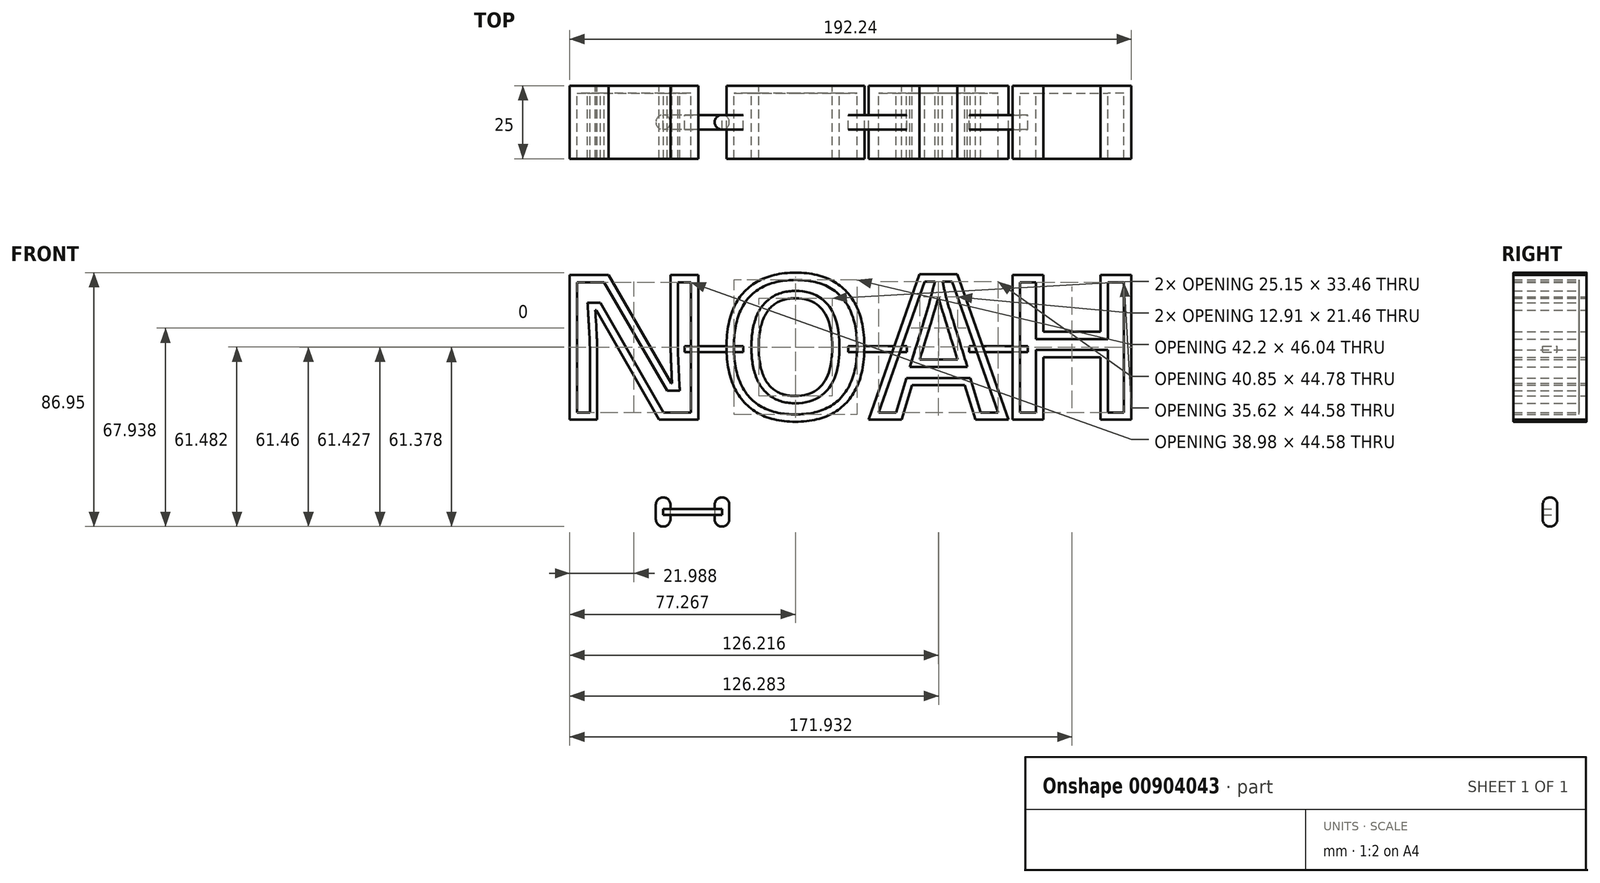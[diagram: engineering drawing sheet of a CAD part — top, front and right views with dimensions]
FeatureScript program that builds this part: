
annotation { "Feature Type Name" : "Feature", "Feature Type Description" : "" }
export const myFeature = defineFeature(function(context is Context, id is Id, definition is map)
    precondition{}
    {
        {
            var Q0;
            Q0=qCreatedBy(makeId("Front.planeOp"),FACE);
            var sketch = newSketch(context, id + "F0", { "sketchPlane" : qUnion([Q0])});
            skText(sketch, "E0", { "text": "O", "fontName": "OpenSans-Bold.ttf"});
            skText(sketch, "E1", { "text": "A", "fontName": "OpenSans-Bold.ttf"});
            skText(sketch, "E2", { "text": "H", "fontName": "OpenSans-Bold.ttf"});
            skText(sketch, "E3", { "text": "N", "fontName": "OpenSans-Bold.ttf"});
            const initialGuessF0  = {"E0": [-0.03252, 0, 1, 0, 0.05], "E1": [0.03031, 0, 1, 0, 0.05], "E2": [0.09753, 0, 1, 0, 0.05], "E3": [-0.10159, 0, 1, 0, 0.05]};
            skSetInitialGuess(sketch, initialGuessF0);
            skSolve(sketch);
        }
        {
            var Q0;
            Q0 = qSketchRegion(id + "F0", true);
            extrude(context, id + "F1", {"entities" : qUnion([Q0]), "endBound" : BoundingType.SYMMETRIC, "depth" : 25 * mm, "offsetDistance" : 25 * mm});
        }
        {
            var Q0;
            Q0=qCreatedBy(makeId("Front.planeOp"),FACE);
            var sketch = newSketch(context, id + "F2", { "sketchPlane" : qUnion([Q0])});
            skLineSegment(sketch, "E4.bottom", {"start": v(-65.87, -26.6) * mm, "end": v(-60.87, -26.6) * mm});
            skLineSegment(sketch, "E4.top", {"start": v(-65.87, -36.6) * mm, "end": v(-60.87, -36.6) * mm});
            skLineSegment(sketch, "E4.left", {"start": v(-65.87, -26.6) * mm, "end": v(-65.87, -36.6) * mm});
            skLineSegment(sketch, "E4.right", {"start": v(-60.87, -26.6) * mm, "end": v(-60.87, -30.6) * mm});
            skLineSegment(sketch, "E5.bottom", {"start": v(-45.73, -26.6) * mm, "end": v(-40.73, -26.6) * mm});
            skLineSegment(sketch, "E5.top", {"start": v(-45.73, -36.6) * mm, "end": v(-40.73, -36.6) * mm});
            skLineSegment(sketch, "E5.left", {"start": v(-45.73, -26.6) * mm, "end": v(-45.73, -30.6) * mm});
            skLineSegment(sketch, "E5.right", {"start": v(-40.73, -26.6) * mm, "end": v(-40.73, -36.6) * mm});
            skLineSegment(sketch, "E6", {"start": v(-63.37, -26.6) * mm, "end": v(-63.37, -36.6) * mm});
            skLineSegment(sketch, "E7", {"start": v(-43.23, -36.6) * mm, "end": v(-43.23, -26.6) * mm});
            skLineSegment(sketch, "E8", {"start": v(-60.87, -30.6) * mm, "end": v(-45.73, -30.6) * mm});
            skLineSegment(sketch, "E9", {"start": v(-60.87, -32.6) * mm, "end": v(-45.73, -32.6) * mm});
            skLineSegment(sketch, "E10.trimOffspring", {"start": v(-60.87, -32.6) * mm, "end": v(-60.87, -36.6) * mm});
            skLineSegment(sketch, "E11.trimOffspring", {"start": v(-45.73, -32.6) * mm, "end": v(-45.73, -36.6) * mm});
            skLineSegment(sketch, "E12", {"start": v(-63.37, -30.6) * mm, "end": v(-43.23, -30.6) * mm});
            skLineSegment(sketch, "E13", {"start": v(-43.23, -32.6) * mm, "end": v(-63.37, -32.6) * mm});
            skSolve(sketch);
        }
        {
            var Q0;
            {var subQ0=sQuery(id+"F2.wireOp",EDGE,"E4.left");Q0=makeQuery(id+"F2.imprint","IMPRINT",FACE,{"disambiguationData":[TD([[makeQuery(id+"F2.imprint","IMPRINT",EDGE,{"derivedFrom":subQ0}),1.0]])]});}
            var Q1;
            Q1=sQuery(id+"F2.wireOp",EDGE,"E6");
            revolve(context, id + "F3", {"surfaceOperationType" : NewSurfaceOperationType.NEW, "entities" : qUnion([Q0]), "axis" : qUnion([Q1]), "revolveType" : RevolveType.FULL});
        }
        {
            var Q0;
            {var subQ0=sQuery(id+"F2.wireOp",EDGE,"E5.right");Q0=makeQuery(id+"F2.imprint","IMPRINT",FACE,{"disambiguationData":[TD([[makeQuery(id+"F2.imprint","IMPRINT",EDGE,{"derivedFrom":subQ0}),-1.0]])]});}
            var Q1;
            Q1=sQuery(id+"F2.wireOp",EDGE,"E7");
            revolve(context, id + "F4", {"surfaceOperationType" : NewSurfaceOperationType.NEW, "entities" : qUnion([Q0]), "axis" : qUnion([Q1]), "revolveType" : RevolveType.FULL});
        }
        {
            var Q0;
            {var subQ0=sQuery(id+"F2.wireOp",EDGE,"E12");var subQ2=sQuery(id+"F2.wireOp",EDGE,"E6");var subQ3=makeQuery(id+"F2.imprint","INTERSECT",VERTEX,{"derivedFrom":[subQ2,subQ0]});Q0=makeQuery(id+"F2.imprint","IMPRINT",FACE,{"disambiguationData":[TD([[makeQuery(id+"F2.imprint","IMPRINT",EDGE,{"disambiguationData":[TD([[subQ3,-1.0]])],"derivedFrom":subQ2}),1.0]])]});}
            extrude(context, id + "F5", {"entities" : qUnion([Q0]), "endBound" : BoundingType.SYMMETRIC, "depth" : 5 * mm, "offsetDistance" : 25 * mm});
        }
        {
            var Q0;
            Q0=makeQuery(id+"F3.opRevolve","SWEPT_FACE",FACE,{"disambiguationData":[OSD([sQuery(id+"F2.wireOp",EDGE,"E4.bottom")])]});
            var Q1;
            Q1=makeQuery(id+"F4.opRevolve","SWEPT_FACE",FACE,{"disambiguationData":[OSD([sQuery(id+"F2.wireOp",EDGE,"E5.bottom")])]});
            var Q2;
            Q2=makeQuery(id+"F4.opRevolve","SWEPT_FACE",FACE,{"disambiguationData":[OSD([sQuery(id+"F2.wireOp",EDGE,"E5.top")])]});
            var Q3;
            Q3=makeQuery(id+"F3.opRevolve","SWEPT_FACE",FACE,{"disambiguationData":[OSD([sQuery(id+"F2.wireOp",EDGE,"E4.top")])]});
            fillet(context, id + "F6", {"entities" : qUnion([Q0, Q1, Q2, Q3]), "radius" : 2.5 * mm, "tangentPropagation" : true, "allowEdgeOverflow" : false});
        }
        {
            var Q0;
            Q0=makeQuery(id+"F5.opExtrude","SWEPT_BODY",BODY,{"disambiguationData":[OSD([sQuery(id+"F2.wireOp",EDGE,"E6"),sQuery(id+"F2.wireOp",EDGE,"E7"),sQuery(id+"F2.wireOp",EDGE,"E12"),sQuery(id+"F2.wireOp",EDGE,"E13")])]});
            transform(context, id + "F7", {"entities" : qUnion([Q0]), "transformType" : TransformType.COPY});
        }
        {
            var Q0;
            Q0=makeQuery(id+"F7.opPattern","COPY",BODY,{"derivedFrom":makeQuery(id+"F5.opExtrude","SWEPT_BODY",BODY,{"disambiguationData":[OSD([sQuery(id+"F2.wireOp",EDGE,"E6"),sQuery(id+"F2.wireOp",EDGE,"E7"),sQuery(id+"F2.wireOp",EDGE,"E12"),sQuery(id+"F2.wireOp",EDGE,"E13")])]}),"instanceName":"1"});
            transform(context, id + "F8", {"entities" : qUnion([Q0]), "transformType" : TransformType.TRANSLATION_3D, "dx" : 7.3 * mm, "dy" : 0 * mm, "dz" : 55.8 * mm, "makeCopy" : false});
        }
        {
            var Q0;
            Q0=makeQuery(id+"F1.opExtrude","SWEPT_BODY",BODY,{"disambiguationData":[OSD([sQuery(id+"F0.wireOp",EDGE,"E0.sketch_text.stroke-0"),sQuery(id+"F0.wireOp",EDGE,"E0.sketch_text.stroke-1"),sQuery(id+"F0.wireOp",EDGE,"E0.sketch_text.stroke-2"),sQuery(id+"F0.wireOp",EDGE,"E0.sketch_text.stroke-3"),sQuery(id+"F0.wireOp",EDGE,"E0.sketch_text.stroke-4"),sQuery(id+"F0.wireOp",EDGE,"E0.sketch_text.stroke-5"),sQuery(id+"F0.wireOp",EDGE,"E0.sketch_text.stroke-6"),sQuery(id+"F0.wireOp",EDGE,"E0.sketch_text.stroke-7"),sQuery(id+"F0.wireOp",EDGE,"E0.sketch_text.stroke-8"),sQuery(id+"F0.wireOp",EDGE,"E0.sketch_text.stroke-9"),sQuery(id+"F0.wireOp",EDGE,"E0.sketch_text.stroke-10"),sQuery(id+"F0.wireOp",EDGE,"E0.sketch_text.stroke-11"),sQuery(id+"F0.wireOp",EDGE,"E0.sketch_text.stroke-12"),sQuery(id+"F0.wireOp",EDGE,"E0.sketch_text.stroke-13")])]});
            transform(context, id + "F9", {"entities" : qUnion([Q0]), "transformType" : TransformType.TRANSLATION_3D, "dx" : -13.2 * mm, "dy" : 0 * mm, "dz" : 0 * mm, "makeCopy" : false});
        }
        {
            var Q0;
            Q0=makeQuery(id+"F7.opPattern","COPY",BODY,{"derivedFrom":makeQuery(id+"F5.opExtrude","SWEPT_BODY",BODY,{"disambiguationData":[OSD([sQuery(id+"F2.wireOp",EDGE,"E6"),sQuery(id+"F2.wireOp",EDGE,"E7"),sQuery(id+"F2.wireOp",EDGE,"E12"),sQuery(id+"F2.wireOp",EDGE,"E13")])]}),"instanceName":"1"});
            transform(context, id + "F10", {"entities" : qUnion([Q0]), "transformType" : TransformType.COPY});
        }
        {
            var Q0;
            Q0=makeQuery(id+"F10.opPattern","COPY",BODY,{"derivedFrom":makeQuery(id+"F7.opPattern","COPY",BODY,{"derivedFrom":makeQuery(id+"F5.opExtrude","SWEPT_BODY",BODY,{"disambiguationData":[OSD([sQuery(id+"F2.wireOp",EDGE,"E6"),sQuery(id+"F2.wireOp",EDGE,"E7"),sQuery(id+"F2.wireOp",EDGE,"E12"),sQuery(id+"F2.wireOp",EDGE,"E13")])]}),"instanceName":"1"}),"instanceName":"1"});
            transform(context, id + "F11", {"entities" : qUnion([Q0]), "transformType" : TransformType.TRANSLATION_3D, "dx" : 56 * mm, "dy" : 0 * mm, "dz" : 0 * mm, "makeCopy" : false});
        }
        {
            var Q0;
            Q0=makeQuery(id+"F1.opExtrude","SWEPT_BODY",BODY,{"disambiguationData":[OSD([sQuery(id+"F0.wireOp",EDGE,"E1.sketch_text.stroke-0"),sQuery(id+"F0.wireOp",EDGE,"E1.sketch_text.stroke-1"),sQuery(id+"F0.wireOp",EDGE,"E1.sketch_text.stroke-2"),sQuery(id+"F0.wireOp",EDGE,"E1.sketch_text.stroke-3"),sQuery(id+"F0.wireOp",EDGE,"E1.sketch_text.stroke-4"),sQuery(id+"F0.wireOp",EDGE,"E1.sketch_text.stroke-5"),sQuery(id+"F0.wireOp",EDGE,"E1.sketch_text.stroke-6"),sQuery(id+"F0.wireOp",EDGE,"E1.sketch_text.stroke-7"),sQuery(id+"F0.wireOp",EDGE,"E1.sketch_text.stroke-8"),sQuery(id+"F0.wireOp",EDGE,"E1.sketch_text.stroke-9"),sQuery(id+"F0.wireOp",EDGE,"E1.sketch_text.stroke-10"),sQuery(id+"F0.wireOp",EDGE,"E1.sketch_text.stroke-11")])]});
            transform(context, id + "F12", {"entities" : qUnion([Q0]), "transformType" : TransformType.TRANSLATION_3D, "dx" : -23.4 * mm, "dy" : 0 * mm, "dz" : 0 * mm, "makeCopy" : false});
        }
        {
            var Q0;
            Q0=makeQuery(id+"F7.opPattern","COPY",BODY,{"derivedFrom":makeQuery(id+"F5.opExtrude","SWEPT_BODY",BODY,{"disambiguationData":[OSD([sQuery(id+"F2.wireOp",EDGE,"E6"),sQuery(id+"F2.wireOp",EDGE,"E7"),sQuery(id+"F2.wireOp",EDGE,"E12"),sQuery(id+"F2.wireOp",EDGE,"E13")])]}),"instanceName":"1"});
            transform(context, id + "F13", {"entities" : qUnion([Q0]), "transformType" : TransformType.COPY});
        }
        {
            var Q0;
            Q0=makeQuery(id+"F13.opPattern","COPY",BODY,{"derivedFrom":makeQuery(id+"F7.opPattern","COPY",BODY,{"derivedFrom":makeQuery(id+"F5.opExtrude","SWEPT_BODY",BODY,{"disambiguationData":[OSD([sQuery(id+"F2.wireOp",EDGE,"E6"),sQuery(id+"F2.wireOp",EDGE,"E7"),sQuery(id+"F2.wireOp",EDGE,"E12"),sQuery(id+"F2.wireOp",EDGE,"E13")])]}),"instanceName":"1"}),"instanceName":"1"});
            transform(context, id + "F14", {"entities" : qUnion([Q0]), "transformType" : TransformType.TRANSLATION_3D, "dx" : 97.4 * mm, "dy" : 0 * mm, "dz" : 0 * mm, "makeCopy" : false});
        }
        {
            var Q0;
            Q0=makeQuery(id+"F1.opExtrude","SWEPT_BODY",BODY,{"disambiguationData":[OSD([sQuery(id+"F0.wireOp",EDGE,"E2.sketch_text.stroke-0"),sQuery(id+"F0.wireOp",EDGE,"E2.sketch_text.stroke-1"),sQuery(id+"F0.wireOp",EDGE,"E2.sketch_text.stroke-2"),sQuery(id+"F0.wireOp",EDGE,"E2.sketch_text.stroke-3"),sQuery(id+"F0.wireOp",EDGE,"E2.sketch_text.stroke-4"),sQuery(id+"F0.wireOp",EDGE,"E2.sketch_text.stroke-5"),sQuery(id+"F0.wireOp",EDGE,"E2.sketch_text.stroke-6"),sQuery(id+"F0.wireOp",EDGE,"E2.sketch_text.stroke-7"),sQuery(id+"F0.wireOp",EDGE,"E2.sketch_text.stroke-8"),sQuery(id+"F0.wireOp",EDGE,"E2.sketch_text.stroke-9"),sQuery(id+"F0.wireOp",EDGE,"E2.sketch_text.stroke-10"),sQuery(id+"F0.wireOp",EDGE,"E2.sketch_text.stroke-11")])]});
            transform(context, id + "F15", {"entities" : qUnion([Q0]), "transformType" : TransformType.TRANSLATION_3D, "dx" : -47.5 * mm, "dy" : 0 * mm, "dz" : 0 * mm, "makeCopy" : false});
        }
        {
            var Q0;
            Q0=makeQuery(id+"F1.opExtrude","CAP_FACE",FACE,{"disambiguationData":[OSD([sQuery(id+"F0.wireOp",EDGE,"E3.sketch_text.stroke-0"),sQuery(id+"F0.wireOp",EDGE,"E3.sketch_text.stroke-1"),sQuery(id+"F0.wireOp",EDGE,"E3.sketch_text.stroke-2"),sQuery(id+"F0.wireOp",EDGE,"E3.sketch_text.stroke-3"),sQuery(id+"F0.wireOp",EDGE,"E3.sketch_text.stroke-4"),sQuery(id+"F0.wireOp",EDGE,"E3.sketch_text.stroke-5"),sQuery(id+"F0.wireOp",EDGE,"E3.sketch_text.stroke-6"),sQuery(id+"F0.wireOp",EDGE,"E3.sketch_text.stroke-7"),sQuery(id+"F0.wireOp",EDGE,"E3.sketch_text.stroke-8"),sQuery(id+"F0.wireOp",EDGE,"E3.sketch_text.stroke-9"),sQuery(id+"F0.wireOp",EDGE,"E3.sketch_text.stroke-10"),sQuery(id+"F0.wireOp",EDGE,"E3.sketch_text.stroke-11"),sQuery(id+"F0.wireOp",EDGE,"E3.sketch_text.stroke-12"),sQuery(id+"F0.wireOp",EDGE,"E3.sketch_text.stroke-13")])],"isStart":false});
            var Q1;
            Q1=makeQuery(id+"F1.opExtrude","CAP_FACE",FACE,{"disambiguationData":[OSD([sQuery(id+"F0.wireOp",EDGE,"E0.sketch_text.stroke-0"),sQuery(id+"F0.wireOp",EDGE,"E0.sketch_text.stroke-1"),sQuery(id+"F0.wireOp",EDGE,"E0.sketch_text.stroke-2"),sQuery(id+"F0.wireOp",EDGE,"E0.sketch_text.stroke-3"),sQuery(id+"F0.wireOp",EDGE,"E0.sketch_text.stroke-4"),sQuery(id+"F0.wireOp",EDGE,"E0.sketch_text.stroke-5"),sQuery(id+"F0.wireOp",EDGE,"E0.sketch_text.stroke-6"),sQuery(id+"F0.wireOp",EDGE,"E0.sketch_text.stroke-7"),sQuery(id+"F0.wireOp",EDGE,"E0.sketch_text.stroke-8"),sQuery(id+"F0.wireOp",EDGE,"E0.sketch_text.stroke-9"),sQuery(id+"F0.wireOp",EDGE,"E0.sketch_text.stroke-10"),sQuery(id+"F0.wireOp",EDGE,"E0.sketch_text.stroke-11"),sQuery(id+"F0.wireOp",EDGE,"E0.sketch_text.stroke-12"),sQuery(id+"F0.wireOp",EDGE,"E0.sketch_text.stroke-13")])],"isStart":false});
            var Q2;
            Q2=makeQuery(id+"F1.opExtrude","CAP_FACE",FACE,{"disambiguationData":[OSD([sQuery(id+"F0.wireOp",EDGE,"E1.sketch_text.stroke-0"),sQuery(id+"F0.wireOp",EDGE,"E1.sketch_text.stroke-1"),sQuery(id+"F0.wireOp",EDGE,"E1.sketch_text.stroke-2"),sQuery(id+"F0.wireOp",EDGE,"E1.sketch_text.stroke-3"),sQuery(id+"F0.wireOp",EDGE,"E1.sketch_text.stroke-4"),sQuery(id+"F0.wireOp",EDGE,"E1.sketch_text.stroke-5"),sQuery(id+"F0.wireOp",EDGE,"E1.sketch_text.stroke-6"),sQuery(id+"F0.wireOp",EDGE,"E1.sketch_text.stroke-7"),sQuery(id+"F0.wireOp",EDGE,"E1.sketch_text.stroke-8"),sQuery(id+"F0.wireOp",EDGE,"E1.sketch_text.stroke-9"),sQuery(id+"F0.wireOp",EDGE,"E1.sketch_text.stroke-10"),sQuery(id+"F0.wireOp",EDGE,"E1.sketch_text.stroke-11")])],"isStart":false});
            var Q3;
            Q3=makeQuery(id+"F1.opExtrude","CAP_FACE",FACE,{"disambiguationData":[OSD([sQuery(id+"F0.wireOp",EDGE,"E2.sketch_text.stroke-0"),sQuery(id+"F0.wireOp",EDGE,"E2.sketch_text.stroke-1"),sQuery(id+"F0.wireOp",EDGE,"E2.sketch_text.stroke-2"),sQuery(id+"F0.wireOp",EDGE,"E2.sketch_text.stroke-3"),sQuery(id+"F0.wireOp",EDGE,"E2.sketch_text.stroke-4"),sQuery(id+"F0.wireOp",EDGE,"E2.sketch_text.stroke-5"),sQuery(id+"F0.wireOp",EDGE,"E2.sketch_text.stroke-6"),sQuery(id+"F0.wireOp",EDGE,"E2.sketch_text.stroke-7"),sQuery(id+"F0.wireOp",EDGE,"E2.sketch_text.stroke-8"),sQuery(id+"F0.wireOp",EDGE,"E2.sketch_text.stroke-9"),sQuery(id+"F0.wireOp",EDGE,"E2.sketch_text.stroke-10"),sQuery(id+"F0.wireOp",EDGE,"E2.sketch_text.stroke-11")])],"isStart":false});
            shell(context, id + "F16", {"entities" : qUnion([Q0, Q1, Q2, Q3]), "thickness" : 2.5 * mm});
        }
    });
